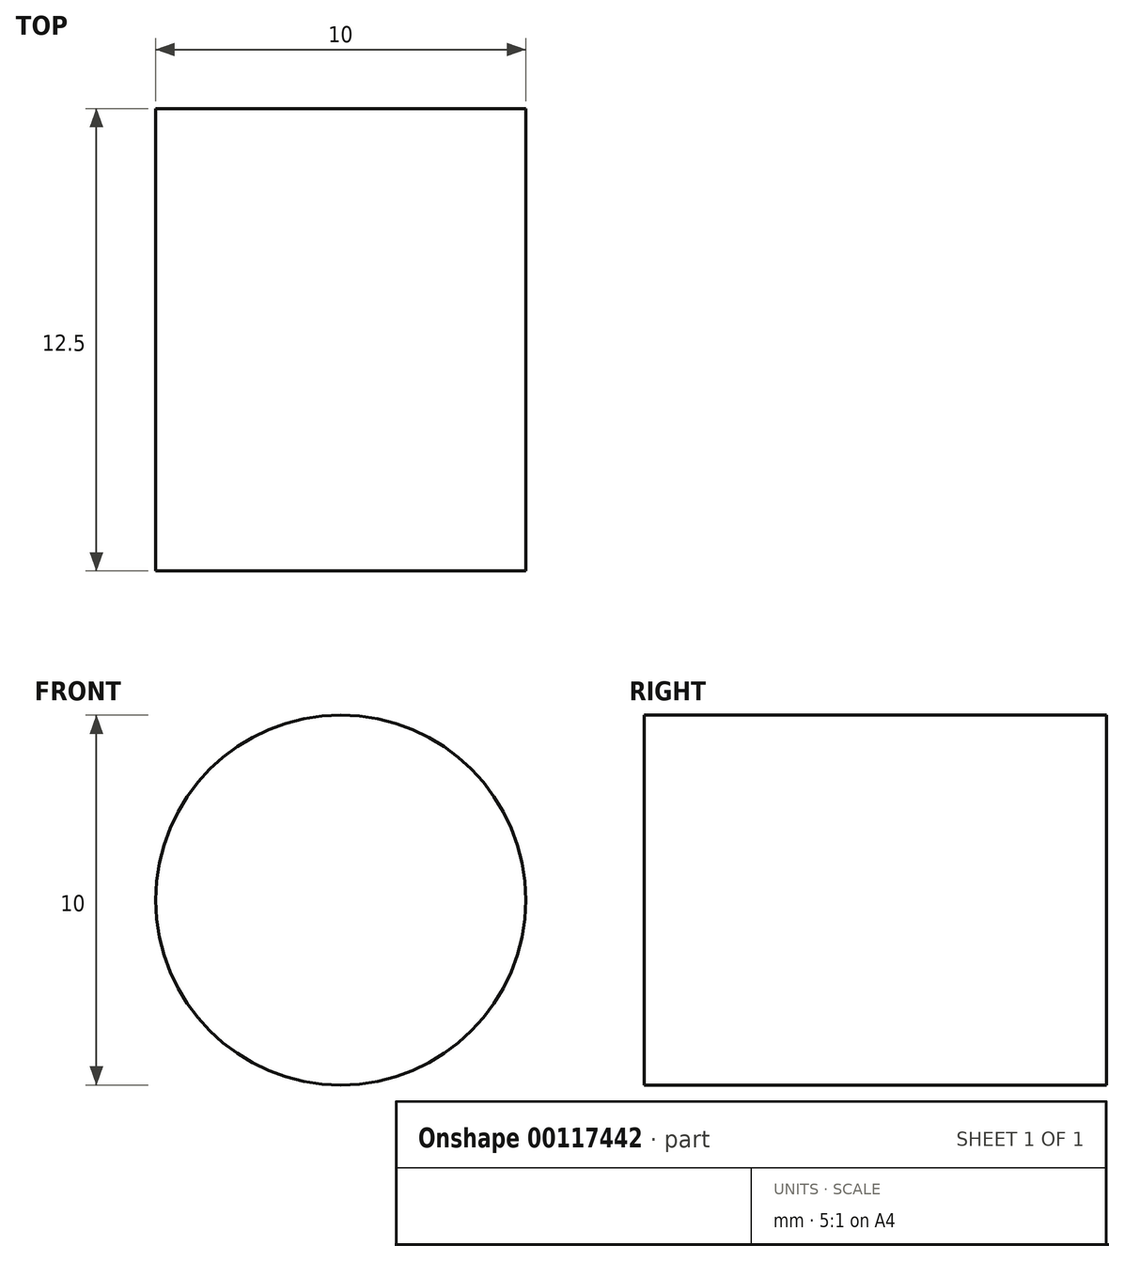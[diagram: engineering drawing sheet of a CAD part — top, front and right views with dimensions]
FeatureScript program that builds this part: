
annotation { "Feature Type Name" : "Feature", "Feature Type Description" : "" }
export const myFeature = defineFeature(function(context is Context, id is Id, definition is map)
    precondition{}
    {
        {
            var Q0;
            Q0=qCreatedBy(makeId("Front.planeOp"),FACE);
            var sketch = newSketch(context, id + "F0", { "sketchPlane" : qUnion([Q0])});
            skCircle(sketch, "E0", {"center": v(0, 0) * mm, "radius": 5 * mm});
            skSolve(sketch);
        }
        {
            var Q0;
            Q0=makeQuery(id+"F0.imprint","IMPRINT",FACE,{"disambiguationData":[TD([[makeQuery(id+"F0.imprint","IMPRINT",EDGE,{"derivedFrom":sQuery(id+"F0.wireOp",EDGE,"E0")}),1.0]])]});
            var Q1;
            Q1=sQuery(id+"F0.wireOp",EDGE,"E0");
            extrude(context, id + "F1", {"entities" : qUnion([Q0]), "surfaceEntities" : qUnion([Q1]), "depth" : 12.5 * mm});
        }
    });
